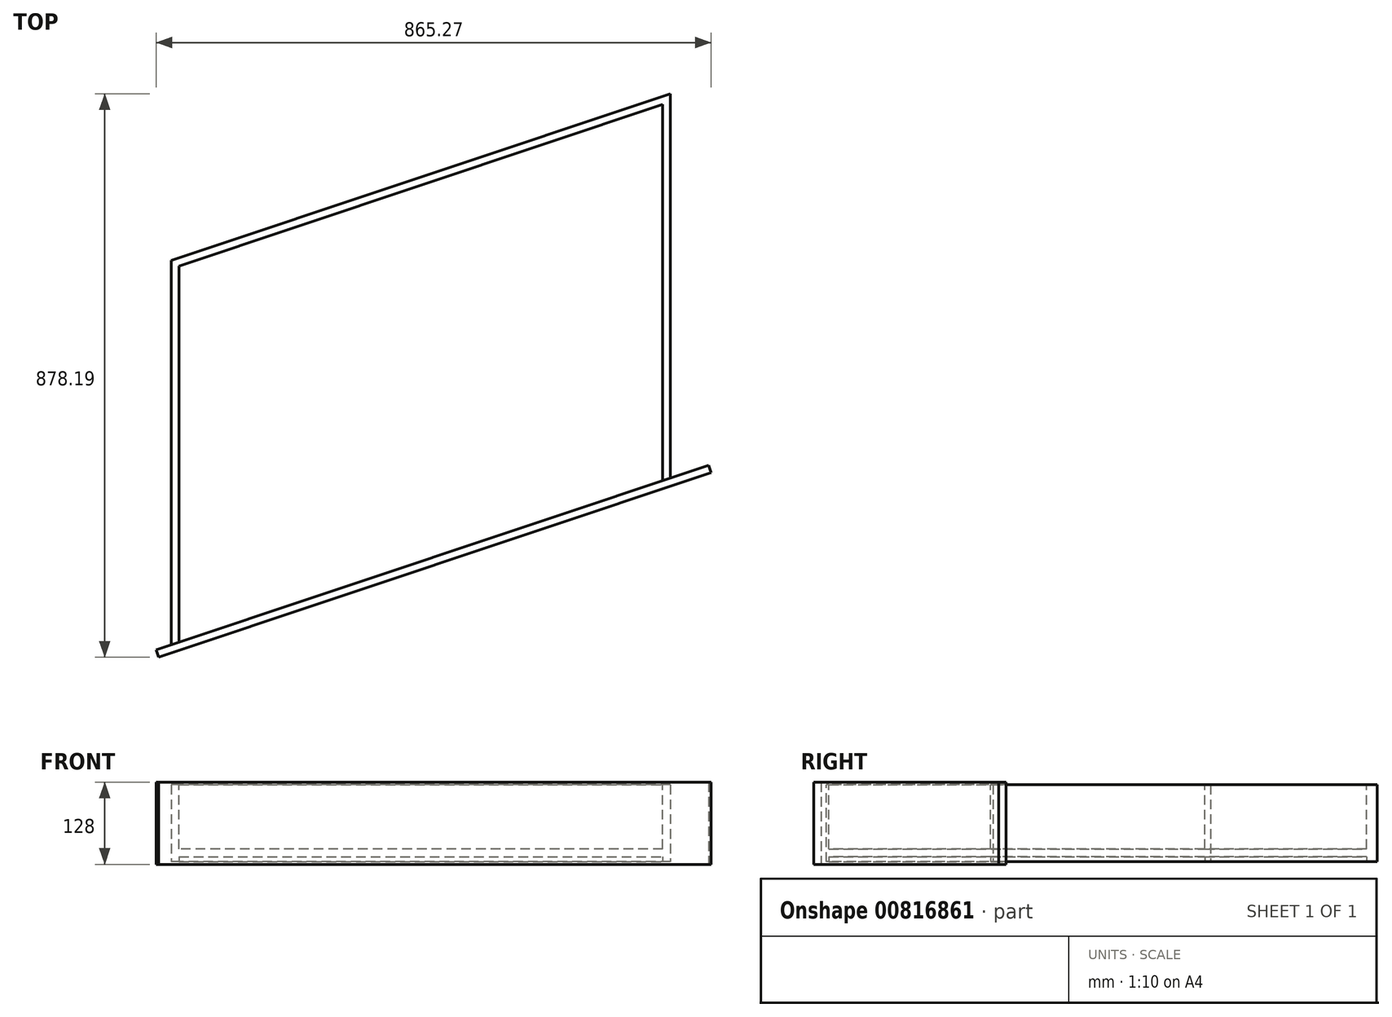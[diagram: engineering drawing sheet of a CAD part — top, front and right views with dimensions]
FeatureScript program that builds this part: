
annotation { "Feature Type Name" : "Feature", "Feature Type Description" : "" }
export const myFeature = defineFeature(function(context is Context, id is Id, definition is map)
    precondition{}
    {
        {
            var Q0;
            Q0=qCreatedBy(makeId("Top.planeOp"),FACE);
            var sketch = newSketch(context, id + "F0", { "sketchPlane" : qUnion([Q0])});
            skLineSegment(sketch, "E0", {"start": v(24.5, -268.47) * mm, "end": v(24.5, -880) * mm});
            skLineSegment(sketch, "E1", {"start": v(24.5, -880) * mm, "end": v(802.5, -620) * mm});
            skLineSegment(sketch, "E2", {"start": v(802.5, -620) * mm, "end": v(802.5, -8.47) * mm});
            skLineSegment(sketch, "E3", {"start": v(802.5, -8.47) * mm, "end": v(24.5, -268.47) * mm});
            skSolve(sketch);
        }
        {
            var Q0;
            Q0 = qSketchRegion(id + "F0", true);
            extrude(context, id + "F1", {"entities" : qUnion([Q0]), "depth" : 120 * mm, "offsetDistance" : 25 * mm});
        }
        {
            var Q0;
            Q0=makeQuery(id+"F1.opExtrude","CAP_FACE",FACE,{"disambiguationData":[OSD([sQuery(id+"F0.wireOp",EDGE,"E0"),sQuery(id+"F0.wireOp",EDGE,"E1"),sQuery(id+"F0.wireOp",EDGE,"E2"),sQuery(id+"F0.wireOp",EDGE,"E3")])],"isStart":true});
            var sketch = newSketch(context, id + "F2", { "sketchPlane" : qUnion([Q0])});
            skLineSegment(sketch, "E4.0", {"start": v(790.5, 25.13) * mm, "end": v(790.5, 611.36) * mm});
            skLineSegment(sketch, "E4.1", {"start": v(36.5, 277.11) * mm, "end": v(790.5, 25.13) * mm});
            skLineSegment(sketch, "E4.2", {"start": v(36.5, 863.34) * mm, "end": v(36.5, 277.11) * mm});
            skLineSegment(sketch, "E4.3", {"start": v(790.5, 611.36) * mm, "end": v(36.5, 863.34) * mm});
            skSolve(sketch);
        }
        {
            var Q0;
            Q0 = qSketchRegion(id + "F2", true);
            extrude(context, id + "F3", {"entities" : qUnion([Q0]), "operationType" : NewBodyOperationType.REMOVE, "oppositeDirection" : true, "depth" : 8 * mm, "offsetDistance" : 25 * mm});
        }
        {
            var Q0;
            Q0=makeQuery(id+"F1.opExtrude","CAP_FACE",FACE,{"disambiguationData":[OSD([sQuery(id+"F0.wireOp",EDGE,"E0"),sQuery(id+"F0.wireOp",EDGE,"E1"),sQuery(id+"F0.wireOp",EDGE,"E2"),sQuery(id+"F0.wireOp",EDGE,"E3")])],"isStart":false});
            var sketch = newSketch(context, id + "F4", { "sketchPlane" : qUnion([Q0])});
            skLineSegment(sketch, "E5.0.0", {"start": v(790.5, -25.13) * mm, "end": v(790.5, -611.36) * mm});
            skLineSegment(sketch, "E5.0.1", {"start": v(790.5, -611.36) * mm, "end": v(36.5, -863.34) * mm});
            skLineSegment(sketch, "E5.0.2", {"start": v(36.5, -863.34) * mm, "end": v(36.5, -277.11) * mm});
            skLineSegment(sketch, "E5.0.3", {"start": v(36.5, -277.11) * mm, "end": v(790.5, -25.13) * mm});
            skSolve(sketch);
        }
        {
            var Q0;
            Q0 = qSketchRegion(id + "F4", true);
            var Q1;
            Q1=makeQuery(id+"F1.opExtrude","SWEPT_BODY",BODY,{"disambiguationData":[OSD([sQuery(id+"F0.wireOp",EDGE,"E0"),sQuery(id+"F0.wireOp",EDGE,"E1"),sQuery(id+"F0.wireOp",EDGE,"E2"),sQuery(id+"F0.wireOp",EDGE,"E3")])]});
            extrude(context, id + "F5", {"entities" : qUnion([Q0]), "operationType" : NewBodyOperationType.REMOVE, "endBound" : BoundingType.UP_TO_BODY, "oppositeDirection" : true, "depth" : 25 * mm, "endBoundEntityBody" : qUnion([Q1]), "hasOffset" : true, "offsetDistance" : 12 * mm});
        }
        {
            var Q0;
            Q0=makeQuery(id+"F1.opExtrude","SWEPT_FACE",FACE,{"disambiguationData":[OSD([sQuery(id+"F0.wireOp",EDGE,"E1")])]});
            var sketch = newSketch(context, id + "F6", { "sketchPlane" : qUnion([Q0])});
            skLineSegment(sketch, "E6.bottom", {"start": v(-276.69, 124) * mm, "end": v(631.6, 124) * mm});
            skLineSegment(sketch, "E6.top", {"start": v(-276.69, -4) * mm, "end": v(631.6, -4) * mm});
            skLineSegment(sketch, "E6.left", {"start": v(-276.69, 124) * mm, "end": v(-276.69, -4) * mm});
            skLineSegment(sketch, "E6.right", {"start": v(631.6, 124) * mm, "end": v(631.6, -4) * mm});
            skSolve(sketch);
        }
        {
            var Q0;
            Q0 = qSketchRegion(id + "F6", true);
            var Q1;
            Q1=makeQuery(id+"F5.boolean.opBoolean","COPY",FACE,{"derivedFrom":makeQuery(id+"F5.opExtrude","SWEPT_FACE",FACE,{"disambiguationData":[OSD([sQuery(id+"F4.wireOp",EDGE,"E5.0.1")])]})});
            extrude(context, id + "F7", {"entities" : qUnion([Q0]), "operationType" : NewBodyOperationType.ADD, "endBound" : BoundingType.UP_TO_SURFACE, "oppositeDirection" : true, "depth" : 25 * mm, "endBoundEntityFace" : qUnion([Q1]), "offsetDistance" : 25 * mm});
        }
    });
